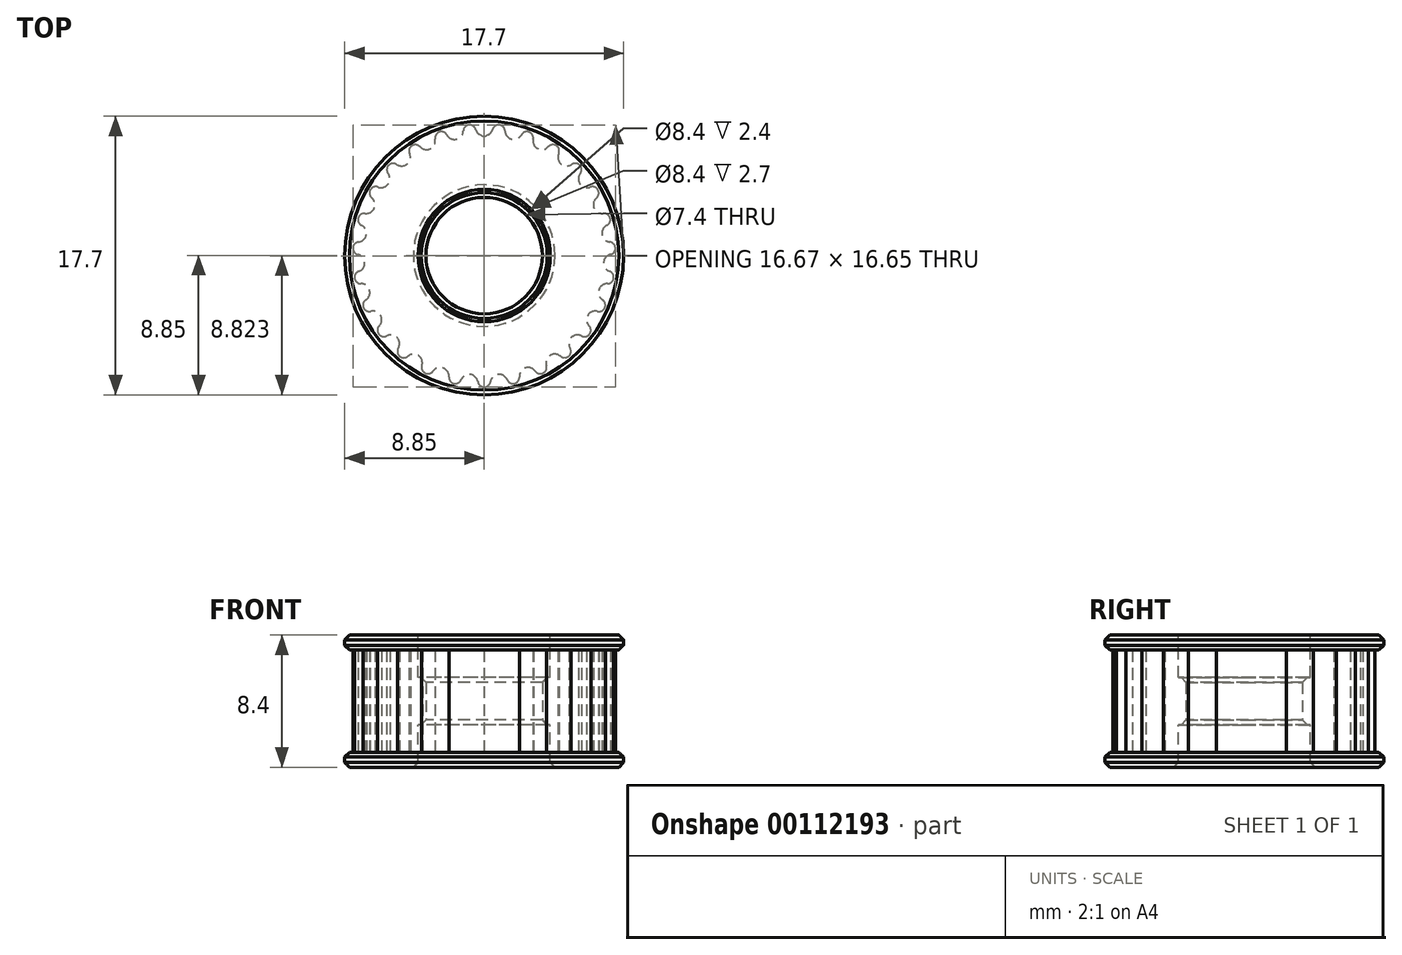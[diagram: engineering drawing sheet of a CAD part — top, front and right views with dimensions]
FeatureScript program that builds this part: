
annotation { "Feature Type Name" : "Feature", "Feature Type Description" : "" }
export const myFeature = defineFeature(function(context is Context, id is Id, definition is map)
    precondition{}
    {
        {
            var Q0;
            Q0=qCreatedBy(makeId("Top.planeOp"),FACE);
            var sketch = newSketch(context, id + "F0", { "sketchPlane" : qUnion([Q0])});
            skCircle(sketch, "E0", {"center": v(0, 0) * mm, "radius": 8.35 * mm});
            skSolve(sketch);
        }
        {
            var Q0;
            Q0 = qSketchRegion(id + "F0", true);
            extrude(context, id + "F1", {"entities" : qUnion([Q0]), "endBound" : BoundingType.SYMMETRIC, "depth" : 7 * mm});
        }
        {
            var Q0;
            Q0=qCreatedBy(makeId("Top.planeOp"),FACE);
            var sketch = newSketch(context, id + "F2", { "sketchPlane" : qUnion([Q0])});
            skArc(sketch, "E1", {"start": v(-0.53, 8) * mm, "mid": v(0, 7.6) * mm, "end": v(0.53, 8) * mm});
            skArc(sketch, "E2", {"start": v(0.97, 8.3) * mm, "mid": v(0.7, 8.23) * mm, "end": v(0.53, 8) * mm});
            skCircle(sketch, "E3", {"center": v(0, 0) * mm, "radius": 7.6 * mm, "construction": true});
            skLineSegment(sketch, "E4", {"start": v(0, 8.16) * mm, "end": v(0, 0) * mm, "construction": true});
            skLineSegment(sketch, "E5", {"start": v(0.92, 7.9) * mm, "end": v(0, 0) * mm, "construction": true});
            skArc(sketch, "E6", {"start": v(0.97, 8.3) * mm, "mid": v(0, 9.13) * mm, "end": v(-0.97, 8.3) * mm});
            skArc(sketch, "E7.trimOffspring", {"start": v(-0.53, 8) * mm, "mid": v(-0.7, 8.23) * mm, "end": v(-0.97, 8.3) * mm});
            skSolve(sketch);
        }
        {
            var Q0;
            Q0 = qSketchRegion(id + "F2", true);
            extrude(context, id + "F3", {"entities" : qUnion([Q0]), "endBound" : BoundingType.SYMMETRIC, "depth" : 6.5 * mm});
        }
        {
            var Q0;
            Q0=makeQuery(id+"F3.opExtrude","SWEPT_BODY",BODY,{"disambiguationData":[OSD([sQuery(id+"F2.wireOp",EDGE,"E1"),sQuery(id+"F2.wireOp",EDGE,"E2"),sQuery(id+"F2.wireOp",EDGE,"E6"),sQuery(id+"F2.wireOp",EDGE,"E7.trimOffspring")])]});
            var Q1;
            Q1=makeQuery(id+"F1.opExtrude","SWEPT_FACE",FACE,{"disambiguationData":[OSD([sQuery(id+"F0.wireOp",EDGE,"E0")])]});
            circularPattern(context, id + "F4", {"operationType" : NewBodyOperationType.REMOVE, "entities" : qUnion([Q0]), "axis" : qUnion([Q1]), "angle" : 360 * degree, "instanceCount" : 27, "equalSpace" : true});
        }
        {
            var Q0;
            Q0=makeQuery(id+"F1.opExtrude","CAP_FACE",FACE,{"disambiguationData":[OSD([sQuery(id+"F0.wireOp",EDGE,"E0")])],"isStart":false});
            var sketch = newSketch(context, id + "F5", { "sketchPlane" : qUnion([Q0])});
            skCircle(sketch, "E8", {"center": v(0, 0) * mm, "radius": 8.85 * mm});
            skSolve(sketch);
        }
        {
            var Q0;
            Q0 = qSketchRegion(id + "F5", true);
            var Q1;
            Q1=makeQuery(id+"F4.boolean.opBoolean","COPY",FACE,{"derivedFrom":makeQuery(id+"F4.opPattern","COPY",FACE,{"derivedFrom":makeQuery(id+"F3.opExtrude","CAP_FACE",FACE,{"disambiguationData":[OSD([sQuery(id+"F2.wireOp",EDGE,"E1"),sQuery(id+"F2.wireOp",EDGE,"E2"),sQuery(id+"F2.wireOp",EDGE,"E6"),sQuery(id+"F2.wireOp",EDGE,"E7.trimOffspring")])],"isStart":false}),"instanceName":"7"})});
            extrude(context, id + "F6", {"entities" : qUnion([Q0]), "operationType" : NewBodyOperationType.ADD, "endBound" : BoundingType.UP_TO_SURFACE, "oppositeDirection" : true, "endBoundEntityFace" : qUnion([Q1]), "depth" : 25 * mm, "hasSecondDirection" : true, "secondDirectionOppositeDirection" : false, "secondDirectionDepth" : .7 * mm});
        }
        {
            var Q0;
            Q0=makeQuery(id+"F1.opExtrude","CAP_FACE",FACE,{"disambiguationData":[OSD([sQuery(id+"F0.wireOp",EDGE,"E0")])],"isStart":true});
            var sketch = newSketch(context, id + "F7", { "sketchPlane" : qUnion([Q0])});
            skCircle(sketch, "E9", {"center": v(0, 0) * mm, "radius": 8.85 * mm});
            skSolve(sketch);
        }
        {
            var Q0;
            Q0 = qSketchRegion(id + "F7", true);
            var Q1;
            Q1=makeQuery(id+"F4.boolean.opBoolean","COPY",FACE,{"derivedFrom":makeQuery(id+"F4.opPattern","COPY",FACE,{"derivedFrom":makeQuery(id+"F3.opExtrude","CAP_FACE",FACE,{"disambiguationData":[OSD([sQuery(id+"F2.wireOp",EDGE,"E1"),sQuery(id+"F2.wireOp",EDGE,"E2"),sQuery(id+"F2.wireOp",EDGE,"E6"),sQuery(id+"F2.wireOp",EDGE,"E7.trimOffspring")])],"isStart":true}),"instanceName":"10"})});
            extrude(context, id + "F8", {"entities" : qUnion([Q0]), "operationType" : NewBodyOperationType.ADD, "endBound" : BoundingType.UP_TO_SURFACE, "oppositeDirection" : true, "endBoundEntityFace" : qUnion([Q1]), "depth" : 25 * mm, "hasSecondDirection" : true, "secondDirectionOppositeDirection" : false, "secondDirectionDepth" : .7 * mm});
        }
        {
            var Q0;
            Q0=makeQuery(id+"F6.opExtrude","CAP_EDGE",EDGE,{"disambiguationData":[OSD([sQuery(id+"F5.wireOp",EDGE,"E8")])],"isStart":false});
            var Q1;
            Q1=makeQuery(id+"F8.opExtrude","CAP_EDGE",EDGE,{"disambiguationData":[OSD([sQuery(id+"F7.wireOp",EDGE,"E9")])],"isStart":false});
            var Q2;
            Q2=makeQuery(id+"F8.opExtrude","CAP_EDGE",EDGE,{"disambiguationData":[OSD([sQuery(id+"F7.wireOp",EDGE,"E9")])],"isStart":true});
            var Q3;
            Q3=makeQuery(id+"F6.opExtrude","CAP_EDGE",EDGE,{"disambiguationData":[OSD([sQuery(id+"F5.wireOp",EDGE,"E8")])],"isStart":true});
            chamfer(context, id + "F9", {"entities" : qUnion([Q0, Q1, Q2, Q3]), "width" : .3 * mm, "tangentPropagation" : true});
        }
        {
            var Q0;
            Q0=makeQuery(id+"F6.opExtrude","CAP_FACE",FACE,{"disambiguationData":[OSD([sQuery(id+"F5.wireOp",EDGE,"E8")])],"isStart":true});
            var sketch = newSketch(context, id + "F10", { "sketchPlane" : qUnion([Q0])});
            skCircle(sketch, "E10", {"center": v(0, 0) * mm, "radius": 4.2 * mm});
            skSolve(sketch);
        }
        {
            var Q0;
            Q0 = qSketchRegion(id + "F10", true);
            extrude(context, id + "F11", {"entities" : qUnion([Q0]), "operationType" : NewBodyOperationType.REMOVE, "endBound" : BoundingType.THROUGH_ALL, "oppositeDirection" : true, "depth" : 25 * mm});
        }
        {
            var Q0;
            Q0=qCreatedBy(makeId("Top.planeOp"),FACE);
            var sketch = newSketch(context, id + "F12", { "sketchPlane" : qUnion([Q0])});
            skCircle(sketch, "E11", {"center": v(0, 0) * mm, "radius": 6 * mm});
            skCircle(sketch, "E12", {"center": v(0, 0) * mm, "radius": 3.7 * mm});
            skSolve(sketch);
        }
        {
            var Q0;
            Q0 = qSketchRegion(id + "F12", true);
            extrude(context, id + "F13", {"entities" : qUnion([Q0]), "operationType" : NewBodyOperationType.ADD, "endBound" : BoundingType.SYMMETRIC, "depth" : 3 * mm});
        }
        {
            var Q0;
            Q0=makeQuery(id+"F13.opExtrude","SWEPT_FACE",FACE,{"disambiguationData":[OSD([sQuery(id+"F12.wireOp",EDGE,"E12")])]});
            var Q1;
            Q1=makeQuery(id+"F11.boolean.opBoolean","COPY",EDGE,{"derivedFrom":makeQuery(id+"F11.opExtrude","CAP_EDGE",EDGE,{"disambiguationData":[OSD([sQuery(id+"F10.wireOp",EDGE,"E10")])],"isStart":true})});
            var Q2;
            Q2=makeQuery(id+"F11.boolean.opBoolean","INTERSECT",EDGE,{"derivedFrom":[makeQuery(id+"F8.opExtrude","CAP_FACE",FACE,{"disambiguationData":[OSD([sQuery(id+"F7.wireOp",EDGE,"E9")])],"isStart":true}),makeQuery(id+"F11.opExtrude","SWEPT_FACE",FACE,{"disambiguationData":[OSD([sQuery(id+"F10.wireOp",EDGE,"E10")])]})]});
            chamfer(context, id + "F14", {"entities" : qUnion([Q0, Q1, Q2]), "width" : .3 * mm, "tangentPropagation" : true});
        }
        {
            var Q0;
            {var subQ0=makeQuery(id+"F3.opExtrude","CAP_FACE",FACE,{"disambiguationData":[OSD([sQuery(id+"F2.wireOp",EDGE,"E1"),sQuery(id+"F2.wireOp",EDGE,"E2"),sQuery(id+"F2.wireOp",EDGE,"E6"),sQuery(id+"F2.wireOp",EDGE,"E7.trimOffspring")])],"isStart":true});Q0=makeQuery(id+"F8.boolean.opBoolean","MERGE",FACE,{"derivedFrom":[makeQuery(id+"F4.boolean.opBoolean","COPY",FACE,{"derivedFrom":subQ0}),makeQuery(id+"F4.boolean.opBoolean","COPY",FACE,{"derivedFrom":makeQuery(id+"F4.opPattern","COPY",FACE,{"derivedFrom":subQ0,"instanceName":"1"})}),makeQuery(id+"F4.boolean.opBoolean","COPY",FACE,{"derivedFrom":makeQuery(id+"F4.opPattern","COPY",FACE,{"derivedFrom":subQ0,"instanceName":"2"})}),makeQuery(id+"F4.boolean.opBoolean","COPY",FACE,{"derivedFrom":makeQuery(id+"F4.opPattern","COPY",FACE,{"derivedFrom":subQ0,"instanceName":"3"})}),makeQuery(id+"F4.boolean.opBoolean","COPY",FACE,{"derivedFrom":makeQuery(id+"F4.opPattern","COPY",FACE,{"derivedFrom":subQ0,"instanceName":"4"})}),makeQuery(id+"F4.boolean.opBoolean","COPY",FACE,{"derivedFrom":makeQuery(id+"F4.opPattern","COPY",FACE,{"derivedFrom":subQ0,"instanceName":"5"})}),makeQuery(id+"F4.boolean.opBoolean","COPY",FACE,{"derivedFrom":makeQuery(id+"F4.opPattern","COPY",FACE,{"derivedFrom":subQ0,"instanceName":"6"})}),makeQuery(id+"F4.boolean.opBoolean","COPY",FACE,{"derivedFrom":makeQuery(id+"F4.opPattern","COPY",FACE,{"derivedFrom":subQ0,"instanceName":"7"})}),makeQuery(id+"F4.boolean.opBoolean","COPY",FACE,{"derivedFrom":makeQuery(id+"F4.opPattern","COPY",FACE,{"derivedFrom":subQ0,"instanceName":"8"})}),makeQuery(id+"F4.boolean.opBoolean","COPY",FACE,{"derivedFrom":makeQuery(id+"F4.opPattern","COPY",FACE,{"derivedFrom":subQ0,"instanceName":"9"})}),makeQuery(id+"F4.boolean.opBoolean","COPY",FACE,{"derivedFrom":makeQuery(id+"F4.opPattern","COPY",FACE,{"derivedFrom":subQ0,"instanceName":"10"})}),makeQuery(id+"F4.boolean.opBoolean","COPY",FACE,{"derivedFrom":makeQuery(id+"F4.opPattern","COPY",FACE,{"derivedFrom":subQ0,"instanceName":"11"})}),makeQuery(id+"F4.boolean.opBoolean","COPY",FACE,{"derivedFrom":makeQuery(id+"F4.opPattern","COPY",FACE,{"derivedFrom":subQ0,"instanceName":"12"})}),makeQuery(id+"F4.boolean.opBoolean","COPY",FACE,{"derivedFrom":makeQuery(id+"F4.opPattern","COPY",FACE,{"derivedFrom":subQ0,"instanceName":"13"})}),makeQuery(id+"F4.boolean.opBoolean","COPY",FACE,{"derivedFrom":makeQuery(id+"F4.opPattern","COPY",FACE,{"derivedFrom":subQ0,"instanceName":"14"})}),makeQuery(id+"F4.boolean.opBoolean","COPY",FACE,{"derivedFrom":makeQuery(id+"F4.opPattern","COPY",FACE,{"derivedFrom":subQ0,"instanceName":"15"})}),makeQuery(id+"F4.boolean.opBoolean","COPY",FACE,{"derivedFrom":makeQuery(id+"F4.opPattern","COPY",FACE,{"derivedFrom":subQ0,"instanceName":"16"})}),makeQuery(id+"F4.boolean.opBoolean","COPY",FACE,{"derivedFrom":makeQuery(id+"F4.opPattern","COPY",FACE,{"derivedFrom":subQ0,"instanceName":"17"})}),makeQuery(id+"F4.boolean.opBoolean","COPY",FACE,{"derivedFrom":makeQuery(id+"F4.opPattern","COPY",FACE,{"derivedFrom":subQ0,"instanceName":"18"})}),makeQuery(id+"F4.boolean.opBoolean","COPY",FACE,{"derivedFrom":makeQuery(id+"F4.opPattern","COPY",FACE,{"derivedFrom":subQ0,"instanceName":"19"})}),makeQuery(id+"F4.boolean.opBoolean","COPY",FACE,{"derivedFrom":makeQuery(id+"F4.opPattern","COPY",FACE,{"derivedFrom":subQ0,"instanceName":"20"})}),makeQuery(id+"F4.boolean.opBoolean","COPY",FACE,{"derivedFrom":makeQuery(id+"F4.opPattern","COPY",FACE,{"derivedFrom":subQ0,"instanceName":"21"})}),makeQuery(id+"F4.boolean.opBoolean","COPY",FACE,{"derivedFrom":makeQuery(id+"F4.opPattern","COPY",FACE,{"derivedFrom":subQ0,"instanceName":"22"})}),makeQuery(id+"F4.boolean.opBoolean","COPY",FACE,{"derivedFrom":makeQuery(id+"F4.opPattern","COPY",FACE,{"derivedFrom":subQ0,"instanceName":"23"})}),makeQuery(id+"F4.boolean.opBoolean","COPY",FACE,{"derivedFrom":makeQuery(id+"F4.opPattern","COPY",FACE,{"derivedFrom":subQ0,"instanceName":"24"})}),makeQuery(id+"F4.boolean.opBoolean","COPY",FACE,{"derivedFrom":makeQuery(id+"F4.opPattern","COPY",FACE,{"derivedFrom":subQ0,"instanceName":"25"})}),makeQuery(id+"F4.boolean.opBoolean","COPY",FACE,{"derivedFrom":makeQuery(id+"F4.opPattern","COPY",FACE,{"derivedFrom":subQ0,"instanceName":"26"})}),makeQuery(id+"F8.opExtrude","CAP_FACE",FACE,{"disambiguationData":[OSD([sQuery(id+"F7.wireOp",EDGE,"E9")])],"isStart":false})]});}
            var sketch = newSketch(context, id + "F15", { "sketchPlane" : qUnion([Q0])});
            skLineSegment(sketch, "E13", {"start": v(0.28, 7.67) * mm, "end": v(0, 7.51) * mm});
            skPoint(sketch, "E13.endSnap0", {"position": v(0, 7.6) * mm});
            skLineSegment(sketch, "E14", {"start": v(0, 7.51) * mm, "end": v(-0.28, 7.67) * mm});
            skLineSegment(sketch, "E15", {"start": v(-0.28, 7.67) * mm, "end": v(0.28, 7.67) * mm});
            skSolve(sketch);
        }
        {
            var Q0;
            Q0 = qSketchRegion(id + "F15", true);
            var Q1;
            {var subQ0=makeQuery(id+"F3.opExtrude","CAP_FACE",FACE,{"disambiguationData":[OSD([sQuery(id+"F2.wireOp",EDGE,"E1"),sQuery(id+"F2.wireOp",EDGE,"E2"),sQuery(id+"F2.wireOp",EDGE,"E6"),sQuery(id+"F2.wireOp",EDGE,"E7.trimOffspring")])],"isStart":false});Q1=makeQuery(id+"F6.boolean.opBoolean","MERGE",FACE,{"derivedFrom":[makeQuery(id+"F4.boolean.opBoolean","COPY",FACE,{"derivedFrom":subQ0}),makeQuery(id+"F4.boolean.opBoolean","COPY",FACE,{"derivedFrom":makeQuery(id+"F4.opPattern","COPY",FACE,{"derivedFrom":subQ0,"instanceName":"1"})}),makeQuery(id+"F4.boolean.opBoolean","COPY",FACE,{"derivedFrom":makeQuery(id+"F4.opPattern","COPY",FACE,{"derivedFrom":subQ0,"instanceName":"2"})}),makeQuery(id+"F4.boolean.opBoolean","COPY",FACE,{"derivedFrom":makeQuery(id+"F4.opPattern","COPY",FACE,{"derivedFrom":subQ0,"instanceName":"3"})}),makeQuery(id+"F4.boolean.opBoolean","COPY",FACE,{"derivedFrom":makeQuery(id+"F4.opPattern","COPY",FACE,{"derivedFrom":subQ0,"instanceName":"4"})}),makeQuery(id+"F4.boolean.opBoolean","COPY",FACE,{"derivedFrom":makeQuery(id+"F4.opPattern","COPY",FACE,{"derivedFrom":subQ0,"instanceName":"5"})}),makeQuery(id+"F4.boolean.opBoolean","COPY",FACE,{"derivedFrom":makeQuery(id+"F4.opPattern","COPY",FACE,{"derivedFrom":subQ0,"instanceName":"6"})}),makeQuery(id+"F4.boolean.opBoolean","COPY",FACE,{"derivedFrom":makeQuery(id+"F4.opPattern","COPY",FACE,{"derivedFrom":subQ0,"instanceName":"7"})}),makeQuery(id+"F4.boolean.opBoolean","COPY",FACE,{"derivedFrom":makeQuery(id+"F4.opPattern","COPY",FACE,{"derivedFrom":subQ0,"instanceName":"8"})}),makeQuery(id+"F4.boolean.opBoolean","COPY",FACE,{"derivedFrom":makeQuery(id+"F4.opPattern","COPY",FACE,{"derivedFrom":subQ0,"instanceName":"9"})}),makeQuery(id+"F4.boolean.opBoolean","COPY",FACE,{"derivedFrom":makeQuery(id+"F4.opPattern","COPY",FACE,{"derivedFrom":subQ0,"instanceName":"10"})}),makeQuery(id+"F4.boolean.opBoolean","COPY",FACE,{"derivedFrom":makeQuery(id+"F4.opPattern","COPY",FACE,{"derivedFrom":subQ0,"instanceName":"11"})}),makeQuery(id+"F4.boolean.opBoolean","COPY",FACE,{"derivedFrom":makeQuery(id+"F4.opPattern","COPY",FACE,{"derivedFrom":subQ0,"instanceName":"12"})}),makeQuery(id+"F4.boolean.opBoolean","COPY",FACE,{"derivedFrom":makeQuery(id+"F4.opPattern","COPY",FACE,{"derivedFrom":subQ0,"instanceName":"13"})}),makeQuery(id+"F4.boolean.opBoolean","COPY",FACE,{"derivedFrom":makeQuery(id+"F4.opPattern","COPY",FACE,{"derivedFrom":subQ0,"instanceName":"14"})}),makeQuery(id+"F4.boolean.opBoolean","COPY",FACE,{"derivedFrom":makeQuery(id+"F4.opPattern","COPY",FACE,{"derivedFrom":subQ0,"instanceName":"15"})}),makeQuery(id+"F4.boolean.opBoolean","COPY",FACE,{"derivedFrom":makeQuery(id+"F4.opPattern","COPY",FACE,{"derivedFrom":subQ0,"instanceName":"16"})}),makeQuery(id+"F4.boolean.opBoolean","COPY",FACE,{"derivedFrom":makeQuery(id+"F4.opPattern","COPY",FACE,{"derivedFrom":subQ0,"instanceName":"17"})}),makeQuery(id+"F4.boolean.opBoolean","COPY",FACE,{"derivedFrom":makeQuery(id+"F4.opPattern","COPY",FACE,{"derivedFrom":subQ0,"instanceName":"18"})}),makeQuery(id+"F4.boolean.opBoolean","COPY",FACE,{"derivedFrom":makeQuery(id+"F4.opPattern","COPY",FACE,{"derivedFrom":subQ0,"instanceName":"19"})}),makeQuery(id+"F4.boolean.opBoolean","COPY",FACE,{"derivedFrom":makeQuery(id+"F4.opPattern","COPY",FACE,{"derivedFrom":subQ0,"instanceName":"20"})}),makeQuery(id+"F4.boolean.opBoolean","COPY",FACE,{"derivedFrom":makeQuery(id+"F4.opPattern","COPY",FACE,{"derivedFrom":subQ0,"instanceName":"21"})}),makeQuery(id+"F4.boolean.opBoolean","COPY",FACE,{"derivedFrom":makeQuery(id+"F4.opPattern","COPY",FACE,{"derivedFrom":subQ0,"instanceName":"22"})}),makeQuery(id+"F4.boolean.opBoolean","COPY",FACE,{"derivedFrom":makeQuery(id+"F4.opPattern","COPY",FACE,{"derivedFrom":subQ0,"instanceName":"23"})}),makeQuery(id+"F4.boolean.opBoolean","COPY",FACE,{"derivedFrom":makeQuery(id+"F4.opPattern","COPY",FACE,{"derivedFrom":subQ0,"instanceName":"24"})}),makeQuery(id+"F4.boolean.opBoolean","COPY",FACE,{"derivedFrom":makeQuery(id+"F4.opPattern","COPY",FACE,{"derivedFrom":subQ0,"instanceName":"25"})}),makeQuery(id+"F4.boolean.opBoolean","COPY",FACE,{"derivedFrom":makeQuery(id+"F4.opPattern","COPY",FACE,{"derivedFrom":subQ0,"instanceName":"26"})}),makeQuery(id+"F6.opExtrude","CAP_FACE",FACE,{"disambiguationData":[OSD([sQuery(id+"F5.wireOp",EDGE,"E8")])],"isStart":false})]});}
            extrude(context, id + "F16", {"entities" : qUnion([Q0]), "operationType" : NewBodyOperationType.REMOVE, "endBound" : BoundingType.UP_TO_SURFACE, "endBoundEntityFace" : qUnion([Q1]), "depth" : 25 * mm});
        }
    });
